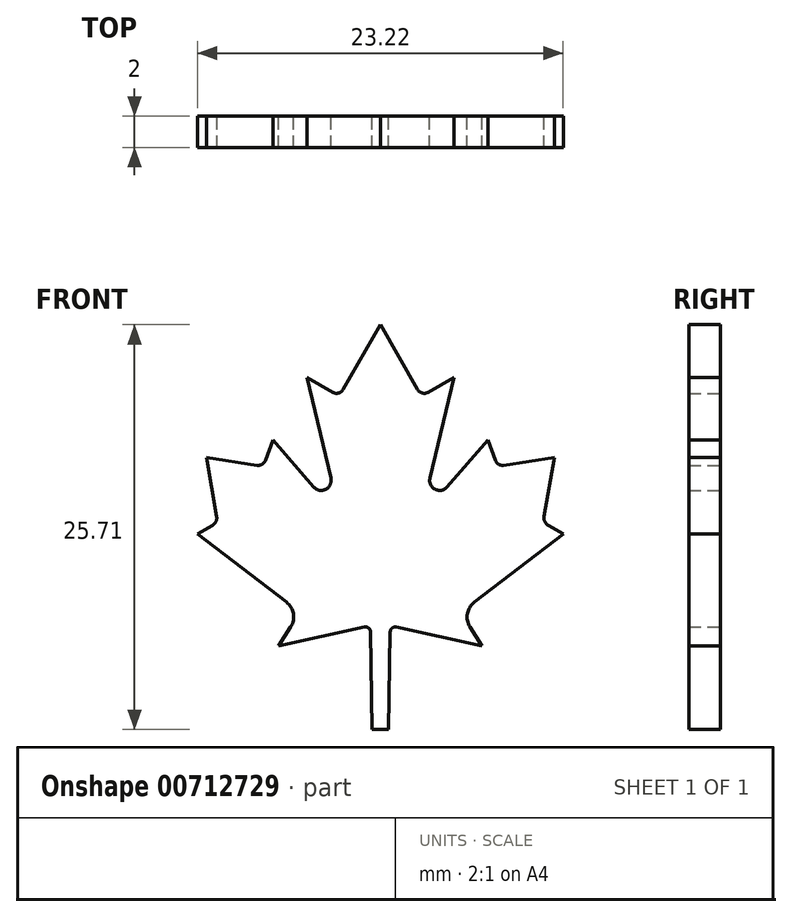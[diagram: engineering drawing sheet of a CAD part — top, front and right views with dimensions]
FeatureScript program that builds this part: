
annotation { "Feature Type Name" : "Feature", "Feature Type Description" : "" }
export const myFeature = defineFeature(function(context is Context, id is Id, definition is map)
    precondition{}
    {
        {
            var Q0;
            Q0=qCreatedBy(makeId("Front.planeOp"),FACE);
            var sketch = newSketch(context, id + "F0", { "sketchPlane" : qUnion([Q0])});
            skLineSegment(sketch, "E0", {"start": v(0.41, 20.57) * mm, "end": v(0.41, -2.04) * mm, "construction": true});
            skLineSegment(sketch, "E1", {"start": v(0.41, 0) * mm, "end": v(0, 0) * mm});
            skArc(sketch, "E2", {"start": v(-2, 17.13) * mm, "mid": v(-1.71, 17.1) * mm, "end": v(-1.48, 17.27) * mm});
            skArc(sketch, "E3", {"start": v(-2.98, 12.32) * mm, "mid": v(-2.37, 12.2) * mm, "end": v(-2.1, 12.77) * mm});
            skLineSegment(sketch, "E4", {"start": v(-5.85, 13.42) * mm, "end": v(-8.43, 13.82) * mm});
            skArc(sketch, "E5", {"start": v(-5.85, 13.42) * mm, "mid": v(-5.6, 13.47) * mm, "end": v(-5.43, 13.67) * mm});
            skLineSegment(sketch, "E6", {"start": v(-8.43, 13.82) * mm, "end": v(-7.9, 10.82) * mm});
            skLineSegment(sketch, "E7", {"start": v(-8.12, 10.37) * mm, "end": v(-8.88, 9.94) * mm});
            skArc(sketch, "E8", {"start": v(-8.12, 10.37) * mm, "mid": v(-7.94, 10.56) * mm, "end": v(-7.9, 10.82) * mm});
            skLineSegment(sketch, "E9", {"start": v(-8.88, 9.94) * mm, "end": v(-4.36, 6.47) * mm});
            skArc(sketch, "E10", {"start": v(-4.14, 5.2) * mm, "mid": v(-4, 5.88) * mm, "end": v(-4.36, 6.47) * mm});
            skLineSegment(sketch, "E11", {"start": v(-4.14, 5.2) * mm, "end": v(-4.75, 4.26) * mm});
            skLineSegment(sketch, "E12", {"start": v(-4.75, 4.26) * mm, "end": v(-0.39, 5.2) * mm});
            skArc(sketch, "E13", {"start": v(-0.09, 4.96) * mm, "mid": v(-0.18, 5.15) * mm, "end": v(-0.39, 5.2) * mm});
            skLineSegment(sketch, "E14", {"start": v(-0.09, 4.96) * mm, "end": v(0, 0) * mm});
            skLineSegment(sketch, "E15", {"start": v(-5.43, 13.67) * mm, "end": v(-5.04, 14.7) * mm});
            skLineSegment(sketch, "E16", {"start": v(-5.04, 14.7) * mm, "end": v(-2.98, 12.32) * mm});
            skLineSegment(sketch, "E17", {"start": v(-3.33, 17.88) * mm, "end": v(-2.1, 12.77) * mm});
            skLineSegment(sketch, "E18", {"start": v(-3.33, 17.88) * mm, "end": v(-2, 17.13) * mm});
            skLineSegment(sketch, "E19", {"start": v(-1.48, 17.27) * mm, "end": v(0.41, 20.57) * mm});
            skLineSegment(sketch, "E20.MirrorCS", {"start": v(2.3, 17.27) * mm, "end": v(0.41, 20.57) * mm});
            skArc(sketch, "E21.MirrorCS", {"start": v(2.83, 17.13) * mm, "mid": v(2.54, 17.1) * mm, "end": v(2.3, 17.27) * mm});
            skLineSegment(sketch, "E22.MirrorCS", {"start": v(4.15, 17.88) * mm, "end": v(2.83, 17.13) * mm});
            skLineSegment(sketch, "E23.MirrorCS", {"start": v(4.15, 17.88) * mm, "end": v(2.93, 12.77) * mm});
            skArc(sketch, "E24.MirrorCS", {"start": v(3.8, 12.32) * mm, "mid": v(3.2, 12.2) * mm, "end": v(2.93, 12.77) * mm});
            skLineSegment(sketch, "E25.MirrorCS", {"start": v(5.87, 14.7) * mm, "end": v(3.8, 12.32) * mm});
            skLineSegment(sketch, "E26.MirrorCS", {"start": v(6.25, 13.67) * mm, "end": v(5.87, 14.7) * mm});
            skArc(sketch, "E27.MirrorCS", {"start": v(6.67, 13.42) * mm, "mid": v(6.42, 13.47) * mm, "end": v(6.25, 13.67) * mm});
            skLineSegment(sketch, "E28.MirrorCS", {"start": v(6.67, 13.42) * mm, "end": v(9.26, 13.82) * mm});
            skLineSegment(sketch, "E29.MirrorCS", {"start": v(9.26, 13.82) * mm, "end": v(8.73, 10.82) * mm});
            skLineSegment(sketch, "E30.MirrorCS", {"start": v(8.94, 10.37) * mm, "end": v(9.7, 9.94) * mm});
            skLineSegment(sketch, "E31.MirrorCS", {"start": v(9.7, 9.94) * mm, "end": v(5.2, 6.47) * mm});
            skArc(sketch, "E32.MirrorCS", {"start": v(8.94, 10.37) * mm, "mid": v(8.77, 10.56) * mm, "end": v(8.73, 10.82) * mm});
            skArc(sketch, "E33.MirrorCS", {"start": v(4.97, 5.2) * mm, "mid": v(4.84, 5.88) * mm, "end": v(5.2, 6.47) * mm});
            skLineSegment(sketch, "E34.MirrorCS", {"start": v(4.97, 5.2) * mm, "end": v(5.58, 4.26) * mm});
            skLineSegment(sketch, "E35.MirrorCS", {"start": v(5.58, 4.26) * mm, "end": v(1.22, 5.2) * mm});
            skArc(sketch, "E36.MirrorCS", {"start": v(0.91, 4.96) * mm, "mid": v(1, 5.15) * mm, "end": v(1.22, 5.2) * mm});
            skLineSegment(sketch, "E37.MirrorCS", {"start": v(0.91, 4.96) * mm, "end": v(0.83, 0) * mm});
            skLineSegment(sketch, "E38", {"start": v(0.41, 0) * mm, "end": v(0.83, 0) * mm});
            skSolve(sketch);
        }
        {
            var Q0;
            Q0=qSketchRegion(id+"F0",true);
            extrude(context, id + "F1", {"entities" : qUnion([Q0]), "depth" : 1.6 * mm, "offsetDistance" : 25 * mm});
        }
        {
            var Q0;
            Q0=makeQuery(id+"F1.opExtrude","SWEPT_BODY",BODY,{"disambiguationData":[OSD([sQuery(id+"F0.wireOp",EDGE,"ed037a27-519c-44da-be8c-65236a3ec034"),sQuery(id+"F0.wireOp",EDGE,"6343007c-e459-43f1-9997-dd42c136c548"),sQuery(id+"F0.wireOp",EDGE,"1510d03a-56f3-4579-be5f-031044057d5a"),sQuery(id+"F0.wireOp",EDGE,"c601d2ca-9eba-4ca6-95fc-8096afe96873"),sQuery(id+"F0.wireOp",EDGE,"ab4ea09d-9808-4047-bbcd-1793a4b746ba"),sQuery(id+"F0.wireOp",EDGE,"11269b72-9e64-4b3b-883a-6b6eb2fb2f51"),sQuery(id+"F0.wireOp",EDGE,"f088e43e-c80c-4ec0-a8d2-5f4e661408ff"),sQuery(id+"F0.wireOp",EDGE,"7d8e27e6-826c-4769-986b-1c248b9e1e73"),sQuery(id+"F0.wireOp",EDGE,"186df18b-654f-49d4-96eb-618ff04dda6f"),sQuery(id+"F0.wireOp",EDGE,"cb1d8b6e-1557-4846-8726-ddbd90911f53"),sQuery(id+"F0.wireOp",EDGE,"44930bef-4081-4419-822d-2ba7e7634c77"),sQuery(id+"F0.wireOp",EDGE,"6393b75a-2cf5-45c7-a483-d64078a40bf6"),sQuery(id+"F0.wireOp",EDGE,"E1"),sQuery(id+"F0.wireOp",EDGE,"b74a8187-764e-416c-afbd-ded604c8d899"),sQuery(id+"F0.wireOp",EDGE,"178de16a-089a-40f1-9e21-f4d6a3dca8d2"),sQuery(id+"F0.wireOp",EDGE,"d272f3bb-a49f-4f1b-8163-c4387b8077ad"),sQuery(id+"F0.wireOp",EDGE,"64fff482-98a1-417a-9e43-e8b62dd7972a"),sQuery(id+"F0.wireOp",EDGE,"9075df64-65b2-4ccf-97c5-b98c4278450a"),sQuery(id+"F0.wireOp",EDGE,"b305cc70-8afa-410b-9c83-ba6d11bd007b"),sQuery(id+"F0.wireOp",EDGE,"db6d278f-af55-4012-9a09-a2fcab609e22"),sQuery(id+"F0.wireOp",EDGE,"E2"),sQuery(id+"F0.wireOp",EDGE,"7b2c1754-6af5-4ccf-85ff-0aa48c990d0e"),sQuery(id+"F0.wireOp",EDGE,"5ca1de30-d1d4-463d-a7a7-dbc791932a40"),sQuery(id+"F0.wireOp",EDGE,"bee27972-3a01-49d6-ad7b-46aec1fb2a49"),sQuery(id+"F0.wireOp",EDGE,"E3"),sQuery(id+"F0.wireOp",EDGE,"4342cadc-fb0f-4cad-8d4e-233cfa2c3e98"),sQuery(id+"F0.wireOp",EDGE,"E4"),sQuery(id+"F0.wireOp",EDGE,"E5"),sQuery(id+"F0.wireOp",EDGE,"E6"),sQuery(id+"F0.wireOp",EDGE,"E7"),sQuery(id+"F0.wireOp",EDGE,"E8"),sQuery(id+"F0.wireOp",EDGE,"E9"),sQuery(id+"F0.wireOp",EDGE,"E10"),sQuery(id+"F0.wireOp",EDGE,"E11"),sQuery(id+"F0.wireOp",EDGE,"E12"),sQuery(id+"F0.wireOp",EDGE,"E13"),sQuery(id+"F0.wireOp",EDGE,"E14"),sQuery(id+"F0.wireOp",EDGE,"38565d54-bfe2-48a1-8056-0ff0d92613e1")])]});
            var Q1;
            Q1=makeQuery(id+"F1.opExtrude","CAP_VERTEX",VERTEX,{"disambiguationData":[OSD([sQuery(id+"F0.wireOp",EDGE,"E37.MirrorCS"),sQuery(id+"F0.wireOp",EDGE,"E38")])],"isStart":false});
            transform(context, id + "F2", {"entities" : qUnion([Q0]), "transformType" : TransformType.SCALE_UNIFORMLY, "scale" : 1.25, "scalePoint" : qUnion([Q1]), "makeCopy" : false});
        }
    });
